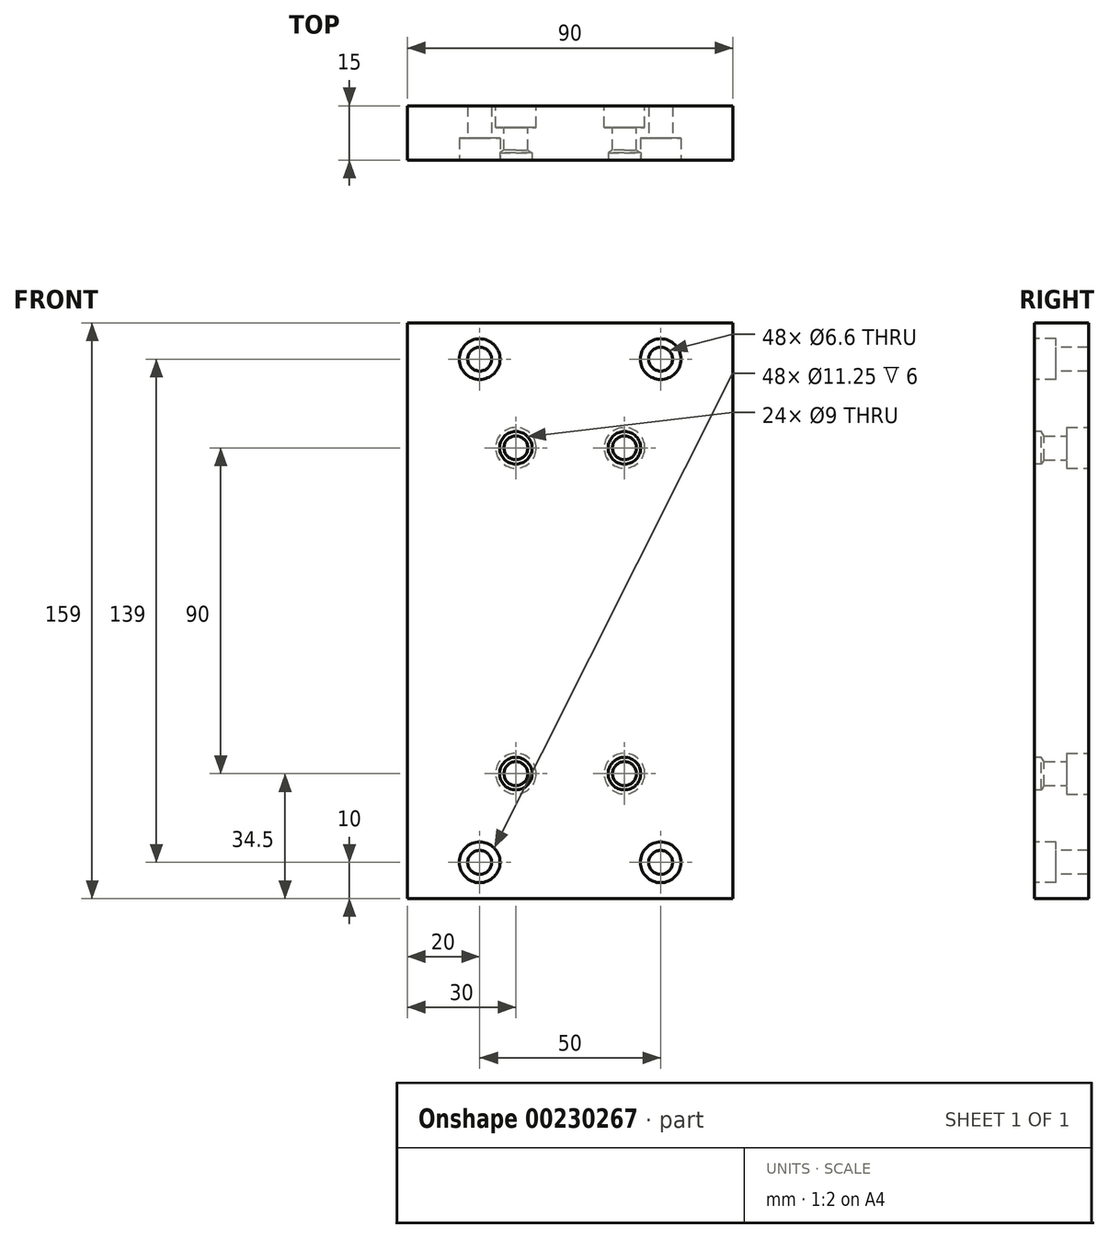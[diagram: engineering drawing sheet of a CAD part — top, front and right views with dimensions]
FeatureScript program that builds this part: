
annotation { "Feature Type Name" : "Feature", "Feature Type Description" : "" }
export const myFeature = defineFeature(function(context is Context, id is Id, definition is map)
    precondition{}
    {
        {
            var Q0;
            Q0=qCreatedBy(makeId("Front.planeOp"),FACE);
            var sketch = newSketch(context, id + "F0", { "sketchPlane" : qUnion([Q0])});
            skLineSegment(sketch, "E0.bottom", {"start": v(45, -79.5) * mm, "end": v(-45, -79.5) * mm});
            skLineSegment(sketch, "E0.top", {"start": v(45, 79.5) * mm, "end": v(-45, 79.5) * mm});
            skLineSegment(sketch, "E0.left", {"start": v(45, -79.5) * mm, "end": v(45, 79.5) * mm});
            skLineSegment(sketch, "E0.right", {"start": v(-45, -79.5) * mm, "end": v(-45, 79.5) * mm});
            skPoint(sketch, "E0.middle", {"position": v(0, 0) * mm});
            skSolve(sketch);
        }
        {
            var Q0;
            Q0=makeQuery(id+"F0.imprint","IMPRINT",FACE,{"disambiguationData":[TD([[makeQuery(id+"F0.imprint","IMPRINT",EDGE,{"derivedFrom":sQuery(id+"F0.wireOp",EDGE,"E0.bottom")}),-1.0]])]});
            extrude(context, id + "F1", {"entities" : qUnion([Q0]), "endBound" : BoundingType.SYMMETRIC, "depth" : 15 * mm});
        }
        {
            var Q0;
            Q0=makeQuery(id+"F1.opExtrude","CAP_FACE",FACE,{"disambiguationData":[OSD([sQuery(id+"F0.wireOp",EDGE,"E0.bottom"),sQuery(id+"F0.wireOp",EDGE,"E0.top"),sQuery(id+"F0.wireOp",EDGE,"E0.left"),sQuery(id+"F0.wireOp",EDGE,"E0.right")])],"isStart":false});
            var sketch = newSketch(context, id + "F2", { "sketchPlane" : qUnion([Q0])});
            skPoint(sketch, "E1", {"position": v(-25, 69.5) * mm});
            skPoint(sketch, "E2", {"position": v(25, 69.5) * mm});
            skPoint(sketch, "E3", {"position": v(25, -69.5) * mm});
            skPoint(sketch, "E4", {"position": v(-25, -69.5) * mm});
            skSolve(sketch);
        }
        {
            var Q0;
            Q0=sQuery(id+"F2.wireOp",VERTEX,"E1");
            var Q1;
            Q1=sQuery(id+"F2.wireOp",VERTEX,"E2");
            var Q2;
            Q2=sQuery(id+"F2.wireOp",VERTEX,"E4");
            var Q3;
            Q3=sQuery(id+"F2.wireOp",VERTEX,"E3");
            var Q4;
            Q4=makeQuery(id+"F1.opExtrude","SWEPT_BODY",BODY,{"disambiguationData":[OSD([sQuery(id+"F0.wireOp",EDGE,"E0.bottom"),sQuery(id+"F0.wireOp",EDGE,"E0.top"),sQuery(id+"F0.wireOp",EDGE,"E0.left"),sQuery(id+"F0.wireOp",EDGE,"E0.right")])]});
            hole(context, id + "F3", {"style" : HoleStyle.C_BORE, "endStyle" : HoleEndStyle.THROUGH, "standardTappedOrClearance" : lookupTablePath({ "standard" : "ISO", "fit" : "Normal", "size" : "M6", "type" : "Clearance" }), "standardBlindInLast" : lookupTablePath({ "fit" : "Standard", "standard" : "ISO", "size" : "M6", "type" : "Clearance" }), "holeDiameter" : 6.6 * mm, "cBoreDiameter" : 11.25 * mm, "cBoreDepth" : 6 * mm, "locations" : qUnion([Q0, Q1, Q2, Q3]), "scope" : qUnion([Q4]), "isTappedThrough" : true});
        }
        {
            var Q0;
            Q0=makeQuery(id+"F1.opExtrude","CAP_FACE",FACE,{"disambiguationData":[OSD([sQuery(id+"F0.wireOp",EDGE,"E0.bottom"),sQuery(id+"F0.wireOp",EDGE,"E0.top"),sQuery(id+"F0.wireOp",EDGE,"E0.left"),sQuery(id+"F0.wireOp",EDGE,"E0.right")])],"isStart":true});
            var sketch = newSketch(context, id + "F4", { "sketchPlane" : qUnion([Q0])});
            skPoint(sketch, "E5", {"position": v(-15, 45) * mm});
            skPoint(sketch, "E6", {"position": v(15, 45) * mm});
            skPoint(sketch, "E7", {"position": v(15, -45) * mm});
            skPoint(sketch, "E8", {"position": v(-15, -45) * mm});
            skSolve(sketch);
        }
        {
            var Q0;
            Q0=sQuery(id+"F4.wireOp",VERTEX,"E5");
            var Q1;
            Q1=sQuery(id+"F4.wireOp",VERTEX,"E6");
            var Q2;
            Q2=sQuery(id+"F4.wireOp",VERTEX,"E7");
            var Q3;
            Q3=sQuery(id+"F4.wireOp",VERTEX,"E8");
            var Q4;
            Q4=makeQuery(id+"F1.opExtrude","SWEPT_BODY",BODY,{"disambiguationData":[OSD([sQuery(id+"F0.wireOp",EDGE,"E0.bottom"),sQuery(id+"F0.wireOp",EDGE,"E0.top"),sQuery(id+"F0.wireOp",EDGE,"E0.left"),sQuery(id+"F0.wireOp",EDGE,"E0.right")])]});
            hole(context, id + "F5", {"style" : HoleStyle.C_BORE, "endStyle" : HoleEndStyle.THROUGH, "standardTappedOrClearance" : lookupTablePath({ "standard" : "ISO", "fit" : "Normal", "size" : "M6", "type" : "Clearance" }), "standardBlindInLast" : lookupTablePath({ "fit" : "Standard", "standard" : "ISO", "size" : "M6", "type" : "Clearance" }), "holeDiameter" : 6.6 * mm, "cBoreDiameter" : 11.25 * mm, "cBoreDepth" : 6 * mm, "locations" : qUnion([Q0, Q1, Q2, Q3]), "scope" : qUnion([Q4]), "isTappedThrough" : true});
        }
        {
            var Q0;
            Q0=makeQuery(id+"F1.opExtrude","CAP_FACE",FACE,{"disambiguationData":[OSD([sQuery(id+"F0.wireOp",EDGE,"E0.bottom"),sQuery(id+"F0.wireOp",EDGE,"E0.top"),sQuery(id+"F0.wireOp",EDGE,"E0.left"),sQuery(id+"F0.wireOp",EDGE,"E0.right")])],"isStart":false});
            var sketch = newSketch(context, id + "F6", { "sketchPlane" : qUnion([Q0])});
            skPoint(sketch, "E9", {"position": v(-15, 45) * mm});
            skPoint(sketch, "E10", {"position": v(15, 45) * mm});
            skPoint(sketch, "E11", {"position": v(15, -45) * mm});
            skPoint(sketch, "E12", {"position": v(-15, -45) * mm});
            skSolve(sketch);
        }
        {
            var Q0;
            Q0=sQuery(id+"F6.wireOp",VERTEX,"E9");
            var Q1;
            Q1=sQuery(id+"F6.wireOp",VERTEX,"E10");
            var Q2;
            Q2=sQuery(id+"F6.wireOp",VERTEX,"E12");
            var Q3;
            Q3=sQuery(id+"F6.wireOp",VERTEX,"E11");
            var Q4;
            Q4=makeQuery(id+"F1.opExtrude","SWEPT_BODY",BODY,{"disambiguationData":[OSD([sQuery(id+"F0.wireOp",EDGE,"E0.bottom"),sQuery(id+"F0.wireOp",EDGE,"E0.top"),sQuery(id+"F0.wireOp",EDGE,"E0.left"),sQuery(id+"F0.wireOp",EDGE,"E0.right")])]});
            hole(context, id + "F7", {"style" : HoleStyle.SIMPLE, "endStyle" : HoleEndStyle.BLIND, "holeDiameter" : 9 * mm, "holeDepth" : 2 * mm, "locations" : qUnion([Q0, Q1, Q2, Q3]), "scope" : qUnion([Q4])});
        }
    });
